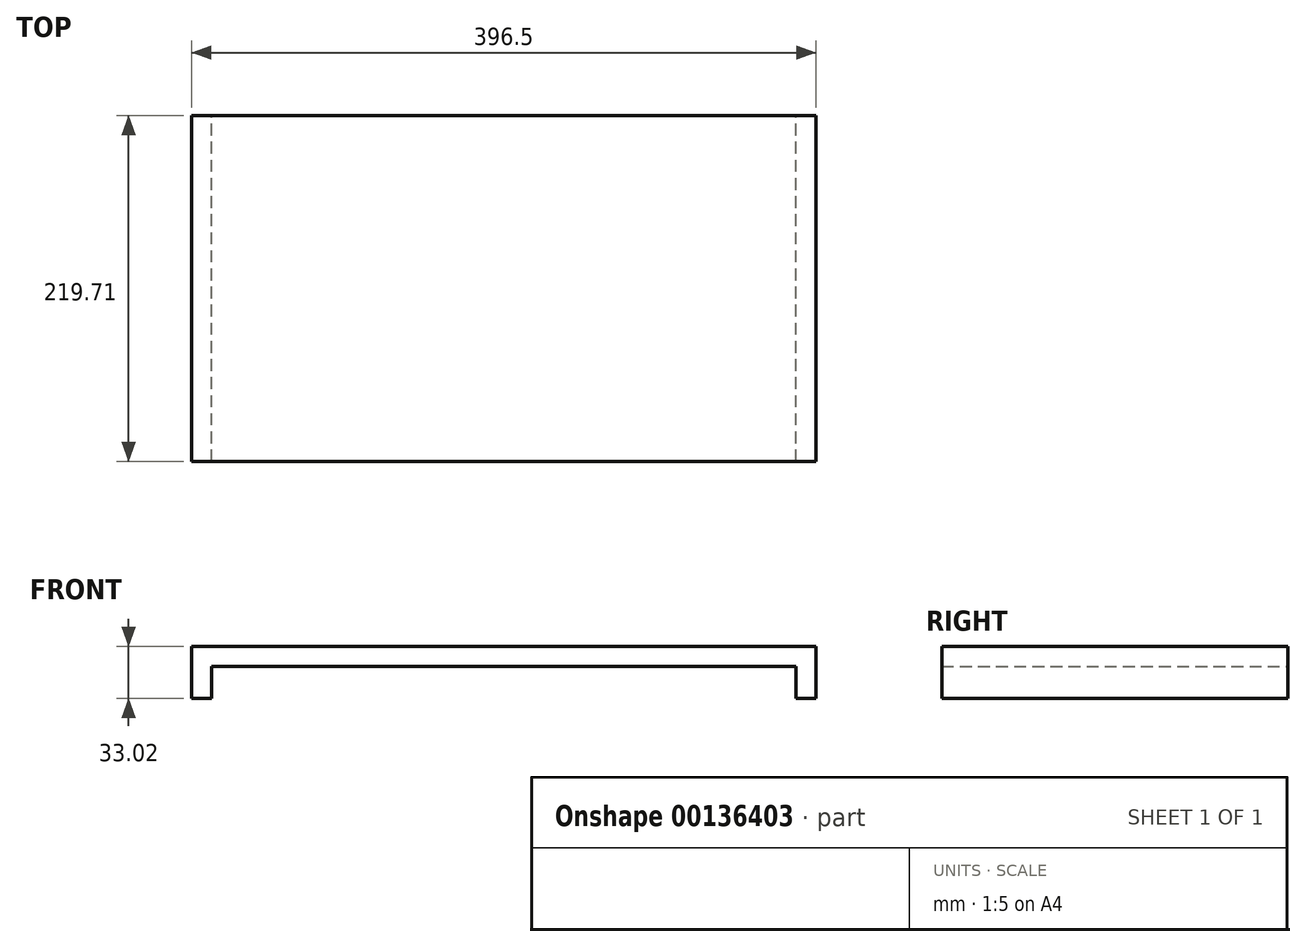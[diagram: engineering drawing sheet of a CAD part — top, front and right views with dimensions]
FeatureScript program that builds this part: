
annotation { "Feature Type Name" : "Feature", "Feature Type Description" : "" }
export const myFeature = defineFeature(function(context is Context, id is Id, definition is map)
    precondition{}
    {
        {
            var Q0;
            Q0=qCreatedBy(makeId("Front.planeOp"),FACE);
            var sketch = newSketch(context, id + "F0", { "sketchPlane" : qUnion([Q0])});
            skLineSegment(sketch, "E0", {"start": v(-235.27, 0) * mm, "end": v(-235.27, 33.02) * mm});
            skLineSegment(sketch, "E1", {"start": v(-235.27, 33.02) * mm, "end": v(161.23, 33.02) * mm});
            skLineSegment(sketch, "E2", {"start": v(161.23, 33.02) * mm, "end": v(161.23, 0) * mm});
            skLineSegment(sketch, "E3.0", {"start": v(148.53, 20.32) * mm, "end": v(148.53, 0) * mm});
            skLineSegment(sketch, "E3.1", {"start": v(-222.57, 20.32) * mm, "end": v(148.53, 20.32) * mm});
            skLineSegment(sketch, "E3.2", {"start": v(-222.57, 0) * mm, "end": v(-222.57, 20.32) * mm});
            skLineSegment(sketch, "E4", {"start": v(-235.27, 0) * mm, "end": v(-222.57, 0) * mm});
            skLineSegment(sketch, "E5", {"start": v(148.53, 0) * mm, "end": v(161.23, 0) * mm});
            skSolve(sketch);
        }
        {
            var Q0;
            Q0=makeQuery(id+"F0.imprint","IMPRINT",FACE,{"disambiguationData":[TD([[makeQuery(id+"F0.imprint","IMPRINT",EDGE,{"derivedFrom":sQuery(id+"F0.wireOp",EDGE,"E0")}),-1.0]])]});
            extrude(context, id + "F1", {"entities" : qUnion([Q0]), "depth" : 219.71 * mm});
        }
    });
